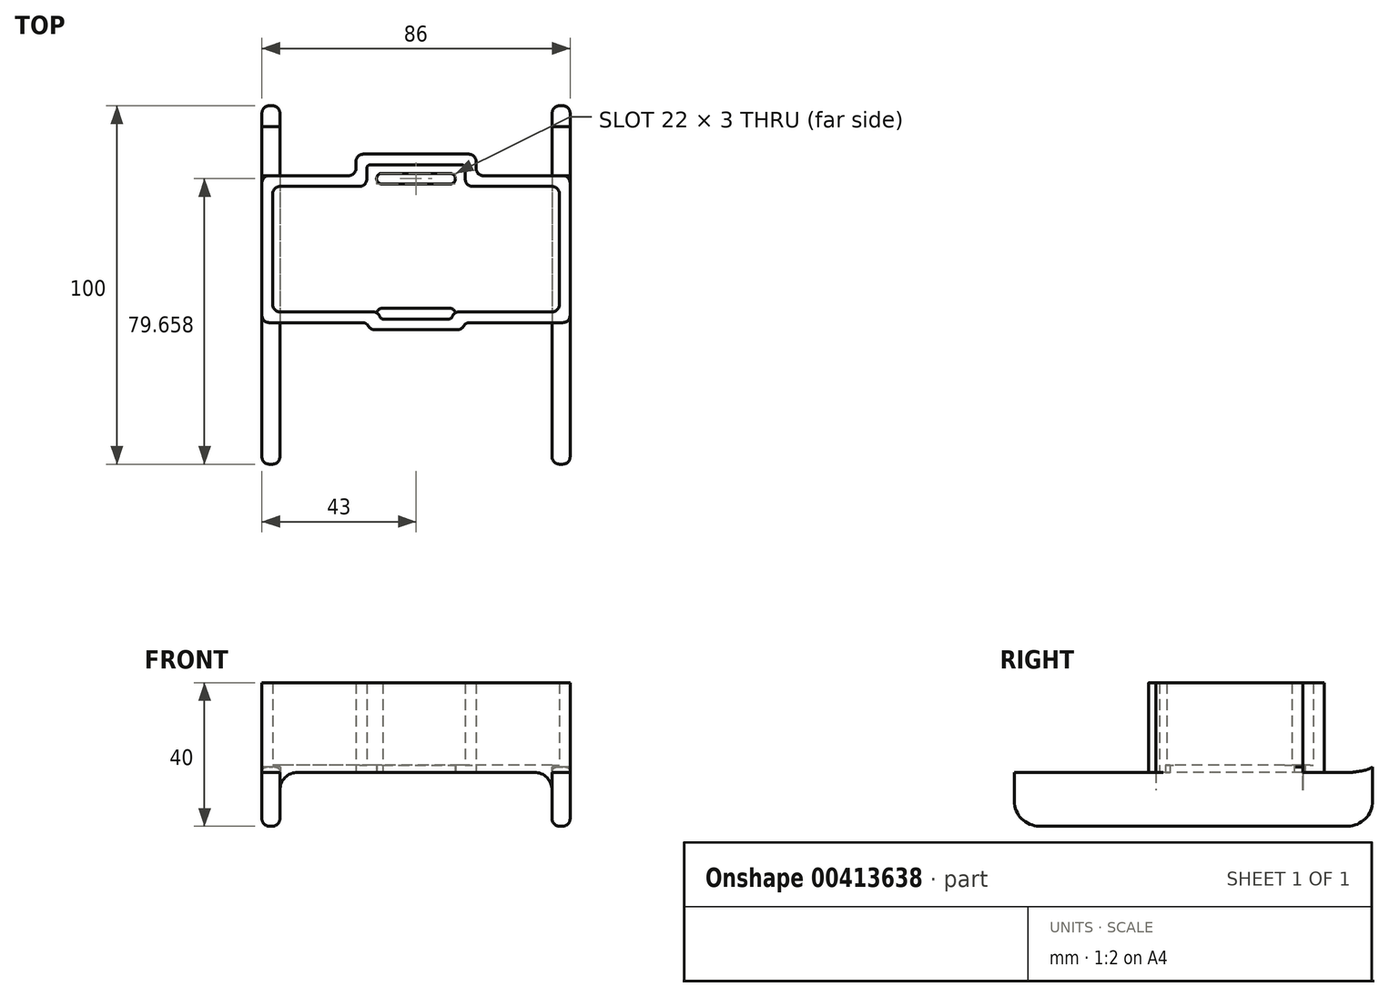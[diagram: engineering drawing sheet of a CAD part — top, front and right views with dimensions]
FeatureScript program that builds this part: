
annotation { "Feature Type Name" : "Feature", "Feature Type Description" : "" }
export const myFeature = defineFeature(function(context is Context, id is Id, definition is map)
    precondition{}
    {
        {
            var Q0;
            Q0=qCreatedBy(makeId("Top.planeOp"),FACE);
            var sketch = newSketch(context, id + "F0", { "sketchPlane" : qUnion([Q0])});
            skLineSegment(sketch, "E0.bottom", {"start": v(38, 17.5) * mm, "end": v(15.75, 17.5) * mm});
            skLineSegment(sketch, "E0.top", {"start": v(38, -17.5) * mm, "end": v(12, -17.5) * mm});
            skLineSegment(sketch, "E0.left", {"start": v(40, 15.5) * mm, "end": v(40, -15.5) * mm});
            skLineSegment(sketch, "E0.right", {"start": v(-40, 15.5) * mm, "end": v(-40, -15.5) * mm});
            skPoint(sketch, "E0.middle", {"position": v(0, 0) * mm});
            skLineSegment(sketch, "E1.0", {"start": v(41, 20.5) * mm, "end": v(18.75, 20.5) * mm});
            skLineSegment(sketch, "E1.1", {"start": v(43, 18.5) * mm, "end": v(43, -18.5) * mm});
            skLineSegment(sketch, "E1.2", {"start": v(41, -20.5) * mm, "end": v(15, -20.5) * mm});
            skLineSegment(sketch, "E1.3", {"start": v(-43, 18.5) * mm, "end": v(-43, -18.5) * mm});
            skLineSegment(sketch, "E2.bottom", {"start": v(12.75, 23.5) * mm, "end": v(-12.75, 23.5) * mm});
            skLineSegment(sketch, "E2.left", {"start": v(13.75, 22.5) * mm, "end": v(13.75, 19.5) * mm});
            skLineSegment(sketch, "E2.right", {"start": v(-13.75, 22.5) * mm, "end": v(-13.75, 19.5) * mm});
            skLineSegment(sketch, "E3.0", {"start": v(-16.75, 24.5) * mm, "end": v(-16.75, 22.5) * mm});
            skLineSegment(sketch, "E3.1", {"start": v(14.75, 26.5) * mm, "end": v(-14.75, 26.5) * mm});
            skLineSegment(sketch, "E3.2", {"start": v(16.75, 24.5) * mm, "end": v(16.75, 22.5) * mm});
            skPoint(sketch, "E2.top.start.orphan", {"position": v(13.75, -23.5) * mm});
            skPoint(sketch, "E4.orphan", {"position": v(-13.75, -23.5) * mm});
            skLineSegment(sketch, "E5", {"start": v(-10, -19.5) * mm, "end": v(-10, -19.5) * mm});
            skLineSegment(sketch, "E6", {"start": v(-9.17, -19.5) * mm, "end": v(9.17, -19.5) * mm});
            skLineSegment(sketch, "E7", {"start": v(10, -19.5) * mm, "end": v(10, -19.5) * mm});
            skLineSegment(sketch, "E8.0", {"start": v(13, -22.5) * mm, "end": v(13, -22.5) * mm});
            skLineSegment(sketch, "E8.1", {"start": v(-11.54, -22.5) * mm, "end": v(11.54, -22.5) * mm});
            skLineSegment(sketch, "E8.2", {"start": v(-13, -22.5) * mm, "end": v(-13, -22.5) * mm});
            skLineSegment(sketch, "E9.trimOffspring", {"start": v(-15, -20.5) * mm, "end": v(-41, -20.5) * mm});
            skLineSegment(sketch, "E10.trimOffspring", {"start": v(-12, -17.5) * mm, "end": v(-38, -17.5) * mm});
            skLineSegment(sketch, "E11.trimOffspring", {"start": v(-18.75, 20.5) * mm, "end": v(-41, 20.5) * mm});
            skLineSegment(sketch, "E12.trimOffspring", {"start": v(-15.75, 17.5) * mm, "end": v(-38, 17.5) * mm});
            skPoint(sketch, "E13.visualSharp", {"position": v(-13.75, 17.5) * mm});
            skArc(sketch, "E13.filletArc", {"start": v(-15.75, 17.5) * mm, "mid": v(-14.34, 18.09) * mm, "end": v(-13.75, 19.5) * mm});
            skPoint(sketch, "E14.visualSharp", {"position": v(13.75, 17.5) * mm});
            skArc(sketch, "E14.filletArc", {"start": v(13.75, 19.5) * mm, "mid": v(14.34, 18.09) * mm, "end": v(15.75, 17.5) * mm});
            skPoint(sketch, "E15.visualSharp", {"position": v(10, -17.5) * mm});
            skArc(sketch, "E15.filletArc", {"start": v(12, -17.5) * mm, "mid": v(10.85, -17.87) * mm, "end": v(10.11, -18.83) * mm});
            skPoint(sketch, "E16.visualSharp", {"position": v(-10, -17.5) * mm});
            skArc(sketch, "E16.filletArc", {"start": v(-10.11, -18.83) * mm, "mid": v(-10.85, -17.87) * mm, "end": v(-12, -17.5) * mm});
            skPoint(sketch, "E17.visualSharp", {"position": v(-13, -20.5) * mm});
            skArc(sketch, "E17.filletArc", {"start": v(-13.27, -21.5) * mm, "mid": v(-14, -20.77) * mm, "end": v(-15, -20.5) * mm});
            skPoint(sketch, "E18.visualSharp", {"position": v(13, -20.5) * mm});
            skArc(sketch, "E18.filletArc", {"start": v(15, -20.5) * mm, "mid": v(14, -20.77) * mm, "end": v(13.27, -21.5) * mm});
            skPoint(sketch, "E19.visualSharp", {"position": v(16.75, 26.5) * mm});
            skArc(sketch, "E19.filletArc", {"start": v(16.75, 24.5) * mm, "mid": v(16.16, 25.91) * mm, "end": v(14.75, 26.5) * mm});
            skPoint(sketch, "E20.visualSharp", {"position": v(-16.75, 26.5) * mm});
            skArc(sketch, "E20.filletArc", {"start": v(-14.75, 26.5) * mm, "mid": v(-16.16, 25.91) * mm, "end": v(-16.75, 24.5) * mm});
            skPoint(sketch, "E21.visualSharp", {"position": v(-16.75, 20.5) * mm});
            skArc(sketch, "E21.filletArc", {"start": v(-18.75, 20.5) * mm, "mid": v(-17.34, 21.09) * mm, "end": v(-16.75, 22.5) * mm});
            skPoint(sketch, "E22.visualSharp", {"position": v(16.75, 20.5) * mm});
            skArc(sketch, "E22.filletArc", {"start": v(16.75, 22.5) * mm, "mid": v(17.34, 21.09) * mm, "end": v(18.75, 20.5) * mm});
            skPoint(sketch, "E23.visualSharp", {"position": v(40, 17.5) * mm});
            skArc(sketch, "E23.filletArc", {"start": v(40, 15.5) * mm, "mid": v(39.41, 16.91) * mm, "end": v(38, 17.5) * mm});
            skPoint(sketch, "E24.visualSharp", {"position": v(43, 20.5) * mm});
            skArc(sketch, "E24.filletArc", {"start": v(43, 18.5) * mm, "mid": v(42.41, 19.91) * mm, "end": v(41, 20.5) * mm});
            skPoint(sketch, "E25.visualSharp", {"position": v(40, -17.5) * mm});
            skArc(sketch, "E25.filletArc", {"start": v(38, -17.5) * mm, "mid": v(39.41, -16.91) * mm, "end": v(40, -15.5) * mm});
            skPoint(sketch, "E26.visualSharp", {"position": v(43, -20.5) * mm});
            skArc(sketch, "E26.filletArc", {"start": v(41, -20.5) * mm, "mid": v(42.41, -19.91) * mm, "end": v(43, -18.5) * mm});
            skPoint(sketch, "E27.visualSharp", {"position": v(-40, -17.5) * mm});
            skArc(sketch, "E27.filletArc", {"start": v(-40, -15.5) * mm, "mid": v(-39.41, -16.91) * mm, "end": v(-38, -17.5) * mm});
            skPoint(sketch, "E28.visualSharp", {"position": v(-43, -20.5) * mm});
            skArc(sketch, "E28.filletArc", {"start": v(-43, -18.5) * mm, "mid": v(-42.41, -19.91) * mm, "end": v(-41, -20.5) * mm});
            skPoint(sketch, "E29.visualSharp", {"position": v(-40, 17.5) * mm});
            skArc(sketch, "E29.filletArc", {"start": v(-38, 17.5) * mm, "mid": v(-39.41, 16.91) * mm, "end": v(-40, 15.5) * mm});
            skPoint(sketch, "E30.visualSharp", {"position": v(-43, 20.5) * mm});
            skArc(sketch, "E30.filletArc", {"start": v(-41, 20.5) * mm, "mid": v(-42.41, 19.91) * mm, "end": v(-43, 18.5) * mm});
            skPoint(sketch, "E31.visualSharp", {"position": v(13.75, 23.5) * mm});
            skArc(sketch, "E31.filletArc", {"start": v(13.75, 22.5) * mm, "mid": v(13.46, 23.2) * mm, "end": v(12.75, 23.5) * mm});
            skPoint(sketch, "E32.visualSharp", {"position": v(-13.75, 23.5) * mm});
            skArc(sketch, "E32.filletArc", {"start": v(-12.75, 23.5) * mm, "mid": v(-13.46, 23.2) * mm, "end": v(-13.75, 22.5) * mm});
            skPoint(sketch, "E33.visualSharp", {"position": v(13, -22.5) * mm});
            skArc(sketch, "E33.filletArc", {"start": v(11.54, -22.5) * mm, "mid": v(12.54, -22.23) * mm, "end": v(13.27, -21.5) * mm});
            skPoint(sketch, "E34.visualSharp", {"position": v(-13, -22.5) * mm});
            skArc(sketch, "E34.filletArc", {"start": v(-13.27, -21.5) * mm, "mid": v(-12.54, -22.23) * mm, "end": v(-11.54, -22.5) * mm});
            skPoint(sketch, "E35.visualSharp", {"position": v(-10, -19.5) * mm});
            skArc(sketch, "E35.filletArc", {"start": v(-10.11, -18.83) * mm, "mid": v(-9.75, -19.32) * mm, "end": v(-9.17, -19.5) * mm});
            skPoint(sketch, "E36.visualSharp", {"position": v(10, -19.5) * mm});
            skArc(sketch, "E36.filletArc", {"start": v(9.17, -19.5) * mm, "mid": v(9.75, -19.32) * mm, "end": v(10.11, -18.83) * mm});
            skArc(sketch, "E37", {"start": v(-9.5, 21.16) * mm, "mid": v(-11, 19.66) * mm, "end": v(-9.5, 18.16) * mm});
            skLineSegment(sketch, "E38", {"start": v(-9.5, 21.16) * mm, "end": v(0, 21.16) * mm});
            skLineSegment(sketch, "E39", {"start": v(-9.5, 18.16) * mm, "end": v(0, 18.16) * mm});
            skLineSegment(sketch, "E40.MirrorCS", {"start": v(9.5, 21.16) * mm, "end": v(0, 21.16) * mm});
            skLineSegment(sketch, "E41.MirrorCS", {"start": v(9.5, 18.16) * mm, "end": v(0, 18.16) * mm});
            skArc(sketch, "E42.MirrorCS", {"start": v(9.5, 21.16) * mm, "mid": v(11, 19.66) * mm, "end": v(9.5, 18.16) * mm});
            skArc(sketch, "E43", {"start": v(-9.2, -19.5) * mm, "mid": v(-9.2, -19.5) * mm, "end": v(-9.2, -19.5) * mm});
            skLineSegment(sketch, "E44", {"start": v(-9.5, -16.53) * mm, "end": v(0, -16.53) * mm});
            skLineSegment(sketch, "E45", {"start": v(-9.2, -19.5) * mm, "end": v(0, -19.5) * mm});
            skLineSegment(sketch, "E46.MirrorCS", {"start": v(9.5, -16.53) * mm, "end": v(0, -16.53) * mm});
            skArc(sketch, "E47.MirrorC", {"start": v(9.5, -16.53) * mm, "mid": v(10.47, -16.88) * mm, "end": v(10.98, -17.78) * mm});
            skArc(sketch, "E48.trimOffspring", {"start": v(-9.5, -16.53) * mm, "mid": v(-10.47, -16.88) * mm, "end": v(-10.98, -17.78) * mm});
            skSolve(sketch);
        }
        {
            var Q0;
            Q0=makeQuery(id+"F0.imprint","IMPRINT",FACE,{"disambiguationData":[TD([[makeQuery(id+"F0.imprint","IMPRINT",EDGE,{"derivedFrom":sQuery(id+"F0.wireOp",EDGE,"E0.bottom")}),1.0]])]});
            extrude(context, id + "F1", {"entities" : qUnion([Q0]), "depth" : 2 * mm});
        }
        {
            var Q0;
            Q0=makeQuery(id+"F0.imprint","IMPRINT",FACE,{"disambiguationData":[TD([[makeQuery(id+"F0.imprint","IMPRINT",EDGE,{"derivedFrom":sQuery(id+"F0.wireOp",EDGE,"E0.bottom")}),-1.0]])]});
            extrude(context, id + "F2", {"entities" : qUnion([Q0]), "operationType" : NewBodyOperationType.ADD, "depth" : 25 * mm});
        }
        {
            var Q0;
            Q0=qCreatedBy(makeId("Top.planeOp"),FACE);
            var sketch = newSketch(context, id + "F3", { "sketchPlane" : qUnion([Q0])});
            skLineSegment(sketch, "E49.bottom", {"start": v(-43, 0) * mm, "end": v(-38, 0) * mm});
            skLineSegment(sketch, "E49.top", {"start": v(-43, -60) * mm, "end": v(-38, -60) * mm});
            skLineSegment(sketch, "E49.left", {"start": v(-43, 0) * mm, "end": v(-43, -60) * mm});
            skLineSegment(sketch, "E49.right", {"start": v(-38, 0) * mm, "end": v(-38, -60) * mm});
            skLineSegment(sketch, "E50.top", {"start": v(-43, 40) * mm, "end": v(-38, 40) * mm});
            skLineSegment(sketch, "E50.left", {"start": v(-43, 0) * mm, "end": v(-43, 40) * mm});
            skLineSegment(sketch, "E50.right", {"start": v(-38, 0) * mm, "end": v(-38, 40) * mm});
            skLineSegment(sketch, "E51.MirrorCS", {"start": v(38, 0) * mm, "end": v(38, -60) * mm});
            skLineSegment(sketch, "E52.MirrorCS", {"start": v(43, -60) * mm, "end": v(38, -60) * mm});
            skLineSegment(sketch, "E53.MirrorCS", {"start": v(43, 0) * mm, "end": v(43, -60) * mm});
            skLineSegment(sketch, "E54.MirrorCS", {"start": v(43, 0) * mm, "end": v(38, 0) * mm});
            skLineSegment(sketch, "E55.MirrorCS", {"start": v(38, 0) * mm, "end": v(38, 40) * mm});
            skLineSegment(sketch, "E56.MirrorCS", {"start": v(43, 0) * mm, "end": v(43, 40) * mm});
            skLineSegment(sketch, "E57.MirrorCS", {"start": v(43, 40) * mm, "end": v(38, 40) * mm});
            skSolve(sketch);
        }
        {
            var Q0;
            Q0=makeQuery(id+"F3.imprint","IMPRINT",FACE,{"disambiguationData":[TD([[makeQuery(id+"F3.imprint","IMPRINT",EDGE,{"derivedFrom":sQuery(id+"F3.wireOp",EDGE,"E49.top")}),1.0]])]});
            var Q1;
            Q1=makeQuery(id+"F3.imprint","IMPRINT",FACE,{"disambiguationData":[TD([[makeQuery(id+"F3.imprint","IMPRINT",EDGE,{"derivedFrom":sQuery(id+"F3.wireOp",EDGE,"E51.MirrorCS")}),1.0]])]});
            extrude(context, id + "F4", {"entities" : qUnion([Q0, Q1]), "operationType" : NewBodyOperationType.ADD, "oppositeDirection" : true, "depth" : 15 * mm});
        }
        {
            var Q0;
            Q0=makeQuery(id+"F3.imprint","IMPRINT",FACE,{"disambiguationData":[TD([[makeQuery(id+"F3.imprint","IMPRINT",EDGE,{"derivedFrom":sQuery(id+"F3.wireOp",EDGE,"E49.bottom")}),1.0]])]});
            var Q1;
            Q1=makeQuery(id+"F3.imprint","IMPRINT",FACE,{"disambiguationData":[TD([[makeQuery(id+"F3.imprint","IMPRINT",EDGE,{"derivedFrom":sQuery(id+"F3.wireOp",EDGE,"E54.MirrorCS")}),-1.0]])]});
            extrude(context, id + "F5", {"entities" : qUnion([Q0, Q1]), "operationType" : NewBodyOperationType.ADD, "oppositeDirection" : true, "depth" : 15 * mm, "hasSecondDirection" : true, "secondDirectionOppositeDirection" : false, "secondDirectionDepth" : 1.5 * mm});
        }
        {
            var Q0;
            Q0=makeQuery(id+"F5.opExtrude","CAP_EDGE",EDGE,{"disambiguationData":[OSD([sQuery(id+"F3.wireOp",EDGE,"E57.MirrorCS")])],"isStart":false});
            var Q1;
            Q1=makeQuery(id+"F5.opExtrude","CAP_EDGE",EDGE,{"disambiguationData":[OSD([sQuery(id+"F3.wireOp",EDGE,"E50.top")])],"isStart":false});
            var Q2;
            Q2=makeQuery(id+"F4.opExtrude","CAP_EDGE",EDGE,{"disambiguationData":[OSD([sQuery(id+"F3.wireOp",EDGE,"E49.top")])],"isStart":false});
            var Q3;
            Q3=makeQuery(id+"F4.opExtrude","CAP_EDGE",EDGE,{"disambiguationData":[OSD([sQuery(id+"F3.wireOp",EDGE,"E52.MirrorCS")])],"isStart":false});
            fillet(context, id + "F6", {"entities" : qUnion([Q0, Q1, Q2, Q3]), "radius" : 7 * mm, "tangentPropagation" : true, "allowEdgeOverflow" : false});
        }
        {
            var Q0;
            Q0=makeQuery(id+"F5.boolean.opBoolean","MERGE",FACE,{"derivedFrom":[makeQuery(id+"F4.opExtrude","SWEPT_FACE",FACE,{"disambiguationData":[OSD([sQuery(id+"F3.wireOp",EDGE,"E49.left")])]}),makeQuery(id+"F5.opExtrude","SWEPT_FACE",FACE,{"disambiguationData":[OSD([sQuery(id+"F3.wireOp",EDGE,"E50.left")])]})]});
            var sketch = newSketch(context, id + "F7", { "sketchPlane" : qUnion([Q0])});
            skFitSpline(sketch, "E58", {"points": [v(-40, 1.5) * mm, v(-38.31, 0.72) * mm, v(-34.24, 0) * mm], "startDerivative": vector(3.68, -2.1) * mm, "endDerivative": vector(7.58, -0.98) * mm});
            skLineSegment(sketch, "E59", {"start": v(-34.24, 0) * mm, "end": v(-26.53, 0) * mm});
            skLineSegment(sketch, "E60", {"start": v(-26.53, 0) * mm, "end": v(-26.53, 1.5) * mm});
            skLineSegment(sketch, "E61", {"start": v(-26.53, 1.5) * mm, "end": v(-40, 1.5) * mm});
            skLineSegment(sketch, "E62", {"start": v(0, 0) * mm, "end": v(-26.53, 0) * mm});
            skLineSegment(sketch, "E63", {"start": v(-26.53, 1.5) * mm, "end": v(0, 1.5) * mm});
            skLineSegment(sketch, "E64", {"start": v(0, 1.5) * mm, "end": v(0, 0) * mm});
            skLineSegment(sketch, "E65", {"start": v(-20.48, 0) * mm, "end": v(-20.48, 1.5) * mm});
            skSolve(sketch);
        }
        {
            var Q0;
            Q0=makeQuery(id+"F7.imprint","IMPRINT",FACE,{"disambiguationData":[TD([[makeQuery(id+"F7.imprint","IMPRINT",EDGE,{"derivedFrom":sQuery(id+"F7.wireOp",EDGE,"E58")}),1.0]])]});
            extrude(context, id + "F8", {"entities" : qUnion([Q0]), "operationType" : NewBodyOperationType.REMOVE, "endBound" : BoundingType.THROUGH_ALL, "oppositeDirection" : true, "depth" : 25 * mm});
        }
        {
            var Q0;
            {var subQ0=sQuery(id+"F7.wireOp",EDGE,"E60");Q0=makeQuery(id+"F7.imprint","IMPRINT",FACE,{"disambiguationData":[TD([[makeQuery(id+"F7.imprint","IMPRINT",EDGE,{"derivedFrom":subQ0}),-1.0]])]});}
            extrude(context, id + "F9", {"entities" : qUnion([Q0]), "operationType" : NewBodyOperationType.REMOVE, "oppositeDirection" : true, "depth" : 5.1 * mm});
        }
        {
            var Q0;
            Q0=makeQuery(id+"F5.boolean.opBoolean","MERGE",FACE,{"derivedFrom":[makeQuery(id+"F4.boolean.opBoolean","MERGE",FACE,{"derivedFrom":[makeQuery(id+"F2.opExtrude","SWEPT_FACE",FACE,{"disambiguationData":[OSD([sQuery(id+"F0.wireOp",EDGE,"E1.1")])]}),makeQuery(id+"F4.opExtrude","SWEPT_FACE",FACE,{"disambiguationData":[OSD([sQuery(id+"F3.wireOp",EDGE,"E53.MirrorCS")])]})]}),makeQuery(id+"F5.opExtrude","SWEPT_FACE",FACE,{"disambiguationData":[OSD([sQuery(id+"F3.wireOp",EDGE,"E56.MirrorCS")])]})]});
            var sketch = newSketch(context, id + "F10", { "sketchPlane" : qUnion([Q0])});
            skLineSegment(sketch, "E66.bottom", {"start": v(26.53, 0) * mm, "end": v(20.53, 0) * mm});
            skLineSegment(sketch, "E66.top", {"start": v(26.53, 1.5) * mm, "end": v(20.53, 1.5) * mm});
            skLineSegment(sketch, "E66.left", {"start": v(26.53, 0) * mm, "end": v(26.53, 1.5) * mm});
            skLineSegment(sketch, "E66.right", {"start": v(20.53, 0) * mm, "end": v(20.53, 1.5) * mm});
            skSolve(sketch);
        }
        {
            var Q0;
            Q0=makeQuery(id+"F10.imprint","IMPRINT",FACE,{"disambiguationData":[TD([[makeQuery(id+"F10.imprint","IMPRINT",EDGE,{"derivedFrom":sQuery(id+"F10.wireOp",EDGE,"E66.bottom")}),-1.0]])]});
            extrude(context, id + "F11", {"entities" : qUnion([Q0]), "operationType" : NewBodyOperationType.REMOVE, "oppositeDirection" : true, "depth" : 5.1 * mm});
        }
        {
            var Q0;
            {var subQ0=sQuery(id+"F0.wireOp",EDGE,"E32.filletArc");var subQ1=sQuery(id+"F0.wireOp",EDGE,"E31.filletArc");var subQ2=sQuery(id+"F0.wireOp",EDGE,"E29.filletArc");var subQ3=sQuery(id+"F0.wireOp",EDGE,"E27.filletArc");var subQ4=sQuery(id+"F0.wireOp",EDGE,"E25.filletArc");var subQ5=sQuery(id+"F0.wireOp",EDGE,"E23.filletArc");var subQ6=sQuery(id+"F0.wireOp",EDGE,"E16.filletArc");var subQ7=sQuery(id+"F0.wireOp",EDGE,"E15.filletArc");var subQ8=sQuery(id+"F0.wireOp",EDGE,"E14.filletArc");var subQ9=sQuery(id+"F0.wireOp",EDGE,"E13.filletArc");var subQ10=sQuery(id+"F0.wireOp",EDGE,"E12.trimOffspring");var subQ11=sQuery(id+"F0.wireOp",EDGE,"E10.trimOffspring");var subQ12=sQuery(id+"F0.wireOp",EDGE,"E2.right");var subQ13=sQuery(id+"F0.wireOp",EDGE,"E2.left");var subQ14=sQuery(id+"F0.wireOp",EDGE,"E2.bottom");var subQ15=sQuery(id+"F0.wireOp",EDGE,"E0.right");var subQ16=sQuery(id+"F0.wireOp",EDGE,"E0.left");var subQ17=sQuery(id+"F0.wireOp",EDGE,"E0.top");var subQ18=sQuery(id+"F0.wireOp",EDGE,"E0.bottom");Q0=makeQuery(id+"F5.boolean.opBoolean","INTERSECT",EDGE,{"derivedFrom":[makeQuery(id+"F2.boolean.opBoolean","MERGE",FACE,{"derivedFrom":[makeQuery(id+"F1.opExtrude","CAP_FACE",FACE,{"disambiguationData":[OSD([subQ18,subQ17,subQ16,subQ15,subQ14,subQ13,subQ12,subQ11,subQ10,subQ9,subQ8,subQ7,subQ6,subQ5,subQ4,subQ3,subQ2,subQ1,subQ0,sQuery(id+"F0.wireOp",EDGE,"E37"),sQuery(id+"F0.wireOp",EDGE,"E38"),sQuery(id+"F0.wireOp",EDGE,"E39"),sQuery(id+"F0.wireOp",EDGE,"E40.MirrorCS"),sQuery(id+"F0.wireOp",EDGE,"E41.MirrorCS"),sQuery(id+"F0.wireOp",EDGE,"E42.MirrorCS"),sQuery(id+"F0.wireOp",EDGE,"E44"),sQuery(id+"F0.wireOp",EDGE,"E46.MirrorCS"),sQuery(id+"F0.wireOp",EDGE,"E47.MirrorC"),sQuery(id+"F0.wireOp",EDGE,"E48.trimOffspring")])],"isStart":true}),makeQuery(id+"F2.opExtrude","CAP_FACE",FACE,{"disambiguationData":[OSD([subQ18,subQ17,subQ16,subQ15,sQuery(id+"F0.wireOp",EDGE,"E1.0"),sQuery(id+"F0.wireOp",EDGE,"E1.1"),sQuery(id+"F0.wireOp",EDGE,"E1.2"),sQuery(id+"F0.wireOp",EDGE,"E1.3"),subQ14,subQ13,subQ12,sQuery(id+"F0.wireOp",EDGE,"E3.0"),sQuery(id+"F0.wireOp",EDGE,"E3.1"),sQuery(id+"F0.wireOp",EDGE,"E3.2"),sQuery(id+"F0.wireOp",EDGE,"E6"),sQuery(id+"F0.wireOp",EDGE,"E8.1"),sQuery(id+"F0.wireOp",EDGE,"E9.trimOffspring"),subQ11,sQuery(id+"F0.wireOp",EDGE,"E11.trimOffspring"),subQ10,subQ9,subQ8,subQ7,subQ6,sQuery(id+"F0.wireOp",EDGE,"E17.filletArc"),sQuery(id+"F0.wireOp",EDGE,"E18.filletArc"),sQuery(id+"F0.wireOp",EDGE,"E19.filletArc"),sQuery(id+"F0.wireOp",EDGE,"E20.filletArc"),sQuery(id+"F0.wireOp",EDGE,"E21.filletArc"),sQuery(id+"F0.wireOp",EDGE,"E22.filletArc"),subQ5,sQuery(id+"F0.wireOp",EDGE,"E24.filletArc"),subQ4,sQuery(id+"F0.wireOp",EDGE,"E26.filletArc"),subQ3,sQuery(id+"F0.wireOp",EDGE,"E28.filletArc"),subQ2,sQuery(id+"F0.wireOp",EDGE,"E30.filletArc"),subQ1,subQ0,sQuery(id+"F0.wireOp",EDGE,"E33.filletArc"),sQuery(id+"F0.wireOp",EDGE,"E34.filletArc"),sQuery(id+"F0.wireOp",EDGE,"E35.filletArc"),sQuery(id+"F0.wireOp",EDGE,"E36.filletArc"),sQuery(id+"F0.wireOp",EDGE,"E43"),sQuery(id+"F0.wireOp",EDGE,"E45")])],"isStart":true})]}),makeQuery(id+"F5.opExtrude","SWEPT_FACE",FACE,{"disambiguationData":[OSD([sQuery(id+"F3.wireOp",EDGE,"E55.MirrorCS")])]})]});}
            var Q1;
            {var subQ0=sQuery(id+"F0.wireOp",EDGE,"E32.filletArc");var subQ1=sQuery(id+"F0.wireOp",EDGE,"E31.filletArc");var subQ2=sQuery(id+"F0.wireOp",EDGE,"E29.filletArc");var subQ3=sQuery(id+"F0.wireOp",EDGE,"E27.filletArc");var subQ4=sQuery(id+"F0.wireOp",EDGE,"E25.filletArc");var subQ5=sQuery(id+"F0.wireOp",EDGE,"E23.filletArc");var subQ6=sQuery(id+"F0.wireOp",EDGE,"E16.filletArc");var subQ7=sQuery(id+"F0.wireOp",EDGE,"E15.filletArc");var subQ8=sQuery(id+"F0.wireOp",EDGE,"E14.filletArc");var subQ9=sQuery(id+"F0.wireOp",EDGE,"E13.filletArc");var subQ10=sQuery(id+"F0.wireOp",EDGE,"E12.trimOffspring");var subQ11=sQuery(id+"F0.wireOp",EDGE,"E10.trimOffspring");var subQ12=sQuery(id+"F0.wireOp",EDGE,"E2.right");var subQ13=sQuery(id+"F0.wireOp",EDGE,"E2.left");var subQ14=sQuery(id+"F0.wireOp",EDGE,"E2.bottom");var subQ15=sQuery(id+"F0.wireOp",EDGE,"E0.right");var subQ16=sQuery(id+"F0.wireOp",EDGE,"E0.left");var subQ17=sQuery(id+"F0.wireOp",EDGE,"E0.top");var subQ18=sQuery(id+"F0.wireOp",EDGE,"E0.bottom");Q1=makeQuery(id+"F9.boolean.opBoolean","SPLIT",EDGE,{"derivedFrom":makeQuery(id+"F5.boolean.opBoolean","INTERSECT",EDGE,{"derivedFrom":[makeQuery(id+"F2.boolean.opBoolean","MERGE",FACE,{"derivedFrom":[makeQuery(id+"F1.opExtrude","CAP_FACE",FACE,{"disambiguationData":[OSD([subQ18,subQ17,subQ16,subQ15,subQ14,subQ13,subQ12,subQ11,subQ10,subQ9,subQ8,subQ7,subQ6,subQ5,subQ4,subQ3,subQ2,subQ1,subQ0,sQuery(id+"F0.wireOp",EDGE,"E37"),sQuery(id+"F0.wireOp",EDGE,"E38"),sQuery(id+"F0.wireOp",EDGE,"E39"),sQuery(id+"F0.wireOp",EDGE,"E40.MirrorCS"),sQuery(id+"F0.wireOp",EDGE,"E41.MirrorCS"),sQuery(id+"F0.wireOp",EDGE,"E42.MirrorCS"),sQuery(id+"F0.wireOp",EDGE,"E44"),sQuery(id+"F0.wireOp",EDGE,"E46.MirrorCS"),sQuery(id+"F0.wireOp",EDGE,"E47.MirrorC"),sQuery(id+"F0.wireOp",EDGE,"E48.trimOffspring")])],"isStart":true}),makeQuery(id+"F2.opExtrude","CAP_FACE",FACE,{"disambiguationData":[OSD([subQ18,subQ17,subQ16,subQ15,sQuery(id+"F0.wireOp",EDGE,"E1.0"),sQuery(id+"F0.wireOp",EDGE,"E1.1"),sQuery(id+"F0.wireOp",EDGE,"E1.2"),sQuery(id+"F0.wireOp",EDGE,"E1.3"),subQ14,subQ13,subQ12,sQuery(id+"F0.wireOp",EDGE,"E3.0"),sQuery(id+"F0.wireOp",EDGE,"E3.1"),sQuery(id+"F0.wireOp",EDGE,"E3.2"),sQuery(id+"F0.wireOp",EDGE,"E6"),sQuery(id+"F0.wireOp",EDGE,"E8.1"),sQuery(id+"F0.wireOp",EDGE,"E9.trimOffspring"),subQ11,sQuery(id+"F0.wireOp",EDGE,"E11.trimOffspring"),subQ10,subQ9,subQ8,subQ7,subQ6,sQuery(id+"F0.wireOp",EDGE,"E17.filletArc"),sQuery(id+"F0.wireOp",EDGE,"E18.filletArc"),sQuery(id+"F0.wireOp",EDGE,"E19.filletArc"),sQuery(id+"F0.wireOp",EDGE,"E20.filletArc"),sQuery(id+"F0.wireOp",EDGE,"E21.filletArc"),sQuery(id+"F0.wireOp",EDGE,"E22.filletArc"),subQ5,sQuery(id+"F0.wireOp",EDGE,"E24.filletArc"),subQ4,sQuery(id+"F0.wireOp",EDGE,"E26.filletArc"),subQ3,sQuery(id+"F0.wireOp",EDGE,"E28.filletArc"),subQ2,sQuery(id+"F0.wireOp",EDGE,"E30.filletArc"),subQ1,subQ0,sQuery(id+"F0.wireOp",EDGE,"E33.filletArc"),sQuery(id+"F0.wireOp",EDGE,"E34.filletArc"),sQuery(id+"F0.wireOp",EDGE,"E35.filletArc"),sQuery(id+"F0.wireOp",EDGE,"E36.filletArc"),sQuery(id+"F0.wireOp",EDGE,"E43"),sQuery(id+"F0.wireOp",EDGE,"E45")])],"isStart":true})]}),makeQuery(id+"F5.opExtrude","SWEPT_FACE",FACE,{"disambiguationData":[OSD([sQuery(id+"F3.wireOp",EDGE,"E50.right")])]})]})});}
            fillet(context, id + "F12", {"entities" : qUnion([Q0, Q1]), "radius" : 5 * mm, "tangentPropagation" : true, "allowEdgeOverflow" : false});
        }
        {
            var Q0;
            Q0=makeQuery(id+"F5.opExtrude","SWEPT_EDGE",EDGE,{"disambiguationData":[OSD([sQuery(id+"F3.wireOp",EDGE,"E50.top"),sQuery(id+"F3.wireOp",EDGE,"E50.right")])]});
            var Q1;
            Q1=makeQuery(id+"F5.opExtrude","SWEPT_EDGE",EDGE,{"disambiguationData":[OSD([sQuery(id+"F3.wireOp",EDGE,"E50.top"),sQuery(id+"F3.wireOp",EDGE,"E50.left")])]});
            var Q2;
            Q2=makeQuery(id+"F5.opExtrude","SWEPT_EDGE",EDGE,{"disambiguationData":[OSD([sQuery(id+"F3.wireOp",EDGE,"E55.MirrorCS"),sQuery(id+"F3.wireOp",EDGE,"E57.MirrorCS")])]});
            var Q3;
            Q3=makeQuery(id+"F5.opExtrude","SWEPT_EDGE",EDGE,{"disambiguationData":[OSD([sQuery(id+"F3.wireOp",EDGE,"E56.MirrorCS"),sQuery(id+"F3.wireOp",EDGE,"E57.MirrorCS")])]});
            fillet(context, id + "F13", {"entities" : qUnion([Q0, Q1, Q2, Q3]), "radius" : 2 * mm, "tangentPropagation" : true, "allowEdgeOverflow" : false});
        }
    });
